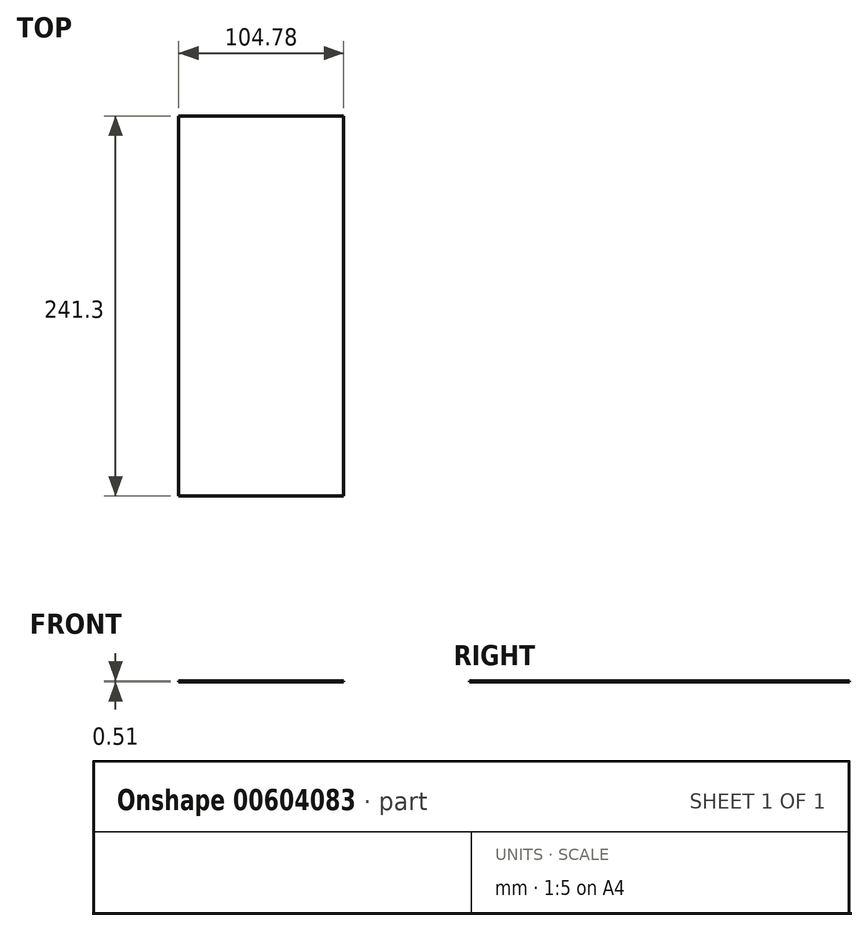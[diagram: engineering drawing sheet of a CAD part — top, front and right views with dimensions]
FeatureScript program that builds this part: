
annotation { "Feature Type Name" : "Feature", "Feature Type Description" : "" }
export const myFeature = defineFeature(function(context is Context, id is Id, definition is map)
    precondition{}
    {
        {
            var Q0;
            Q0=qCreatedBy(makeId("Top.planeOp"),FACE);
            var sketch = newSketch(context, id + "F0", { "sketchPlane" : qUnion([Q0])});
            skLineSegment(sketch, "E0.bottom", {"start": v(52.39, 120.65) * mm, "end": v(-52.39, 120.65) * mm});
            skLineSegment(sketch, "E0.top", {"start": v(52.39, -120.65) * mm, "end": v(-52.39, -120.65) * mm});
            skLineSegment(sketch, "E0.left", {"start": v(52.39, 120.65) * mm, "end": v(52.39, -120.65) * mm});
            skLineSegment(sketch, "E0.right", {"start": v(-52.39, 120.65) * mm, "end": v(-52.39, -120.65) * mm});
            skPoint(sketch, "E0.middle", {"position": v(0, 0) * mm});
            skSolve(sketch);
        }
        {
            var Q0;
            Q0 = qSketchRegion(id + "F0", true);
            extrude(context, id + "F1", {"entities" : qUnion([Q0]), "depth" : 0.5 * mm, "offsetDistance" : 25.4 * mm});
        }
    });
